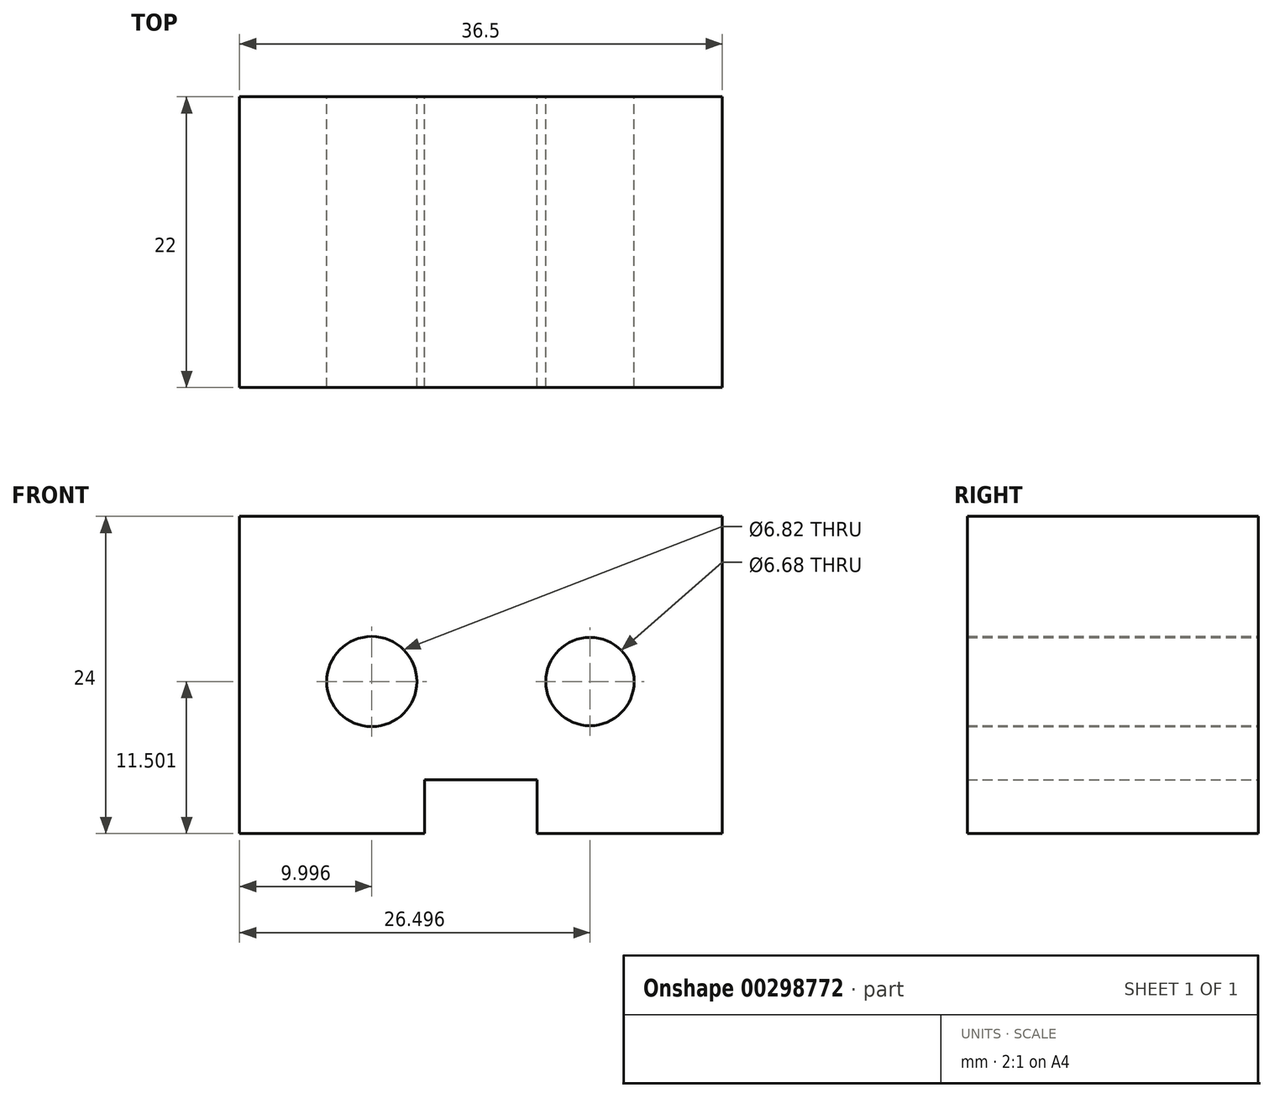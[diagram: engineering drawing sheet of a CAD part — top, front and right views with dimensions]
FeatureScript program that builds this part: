
annotation { "Feature Type Name" : "Feature", "Feature Type Description" : "" }
export const myFeature = defineFeature(function(context is Context, id is Id, definition is map)
    precondition{}
    {
        {
            var Q0;
            Q0=qCreatedBy(makeId("Front.planeOp"),FACE);
            var sketch = newSketch(context, id + "F0", { "sketchPlane" : qUnion([Q0])});
            skLineSegment(sketch, "E0", {"start": v(-57.45, 37.25) * mm, "end": v(-57.45, 13.25) * mm});
            skLineSegment(sketch, "E1", {"start": v(-57.45, 37.25) * mm, "end": v(-20.95, 37.25) * mm});
            skLineSegment(sketch, "E2", {"start": v(-57.45, 13.25) * mm, "end": v(-43.45, 13.25) * mm});
            skLineSegment(sketch, "E3", {"start": v(-43.45, 13.25) * mm, "end": v(-43.45, 17.3) * mm});
            skLineSegment(sketch, "E4", {"start": v(-43.45, 17.3) * mm, "end": v(-34.95, 17.3) * mm});
            skLineSegment(sketch, "E5", {"start": v(-20.95, 37.25) * mm, "end": v(-20.95, 13.25) * mm});
            skLineSegment(sketch, "E6", {"start": v(-20.95, 13.25) * mm, "end": v(-34.95, 13.25) * mm});
            skLineSegment(sketch, "E7", {"start": v(-34.95, 17.3) * mm, "end": v(-34.95, 13.25) * mm});
            skPoint(sketch, "E8", {"position": v(-47.45, 24.75) * mm});
            skCircle(sketch, "E9", {"center": v(-47.45, 24.75) * mm, "radius": 3.4 * mm});
            skPoint(sketch, "E10", {"position": v(-30.95, 24.75) * mm});
            skCircle(sketch, "E11", {"center": v(-30.95, 24.75) * mm, "radius": 3.34 * mm});
            skSolve(sketch);
        }
        {
            var Q0;
            Q0 = qSketchRegion(id + "F0", true);
            extrude(context, id + "F1", {"entities" : qUnion([Q0]), "depth" : 22 * mm});
        }
    });
